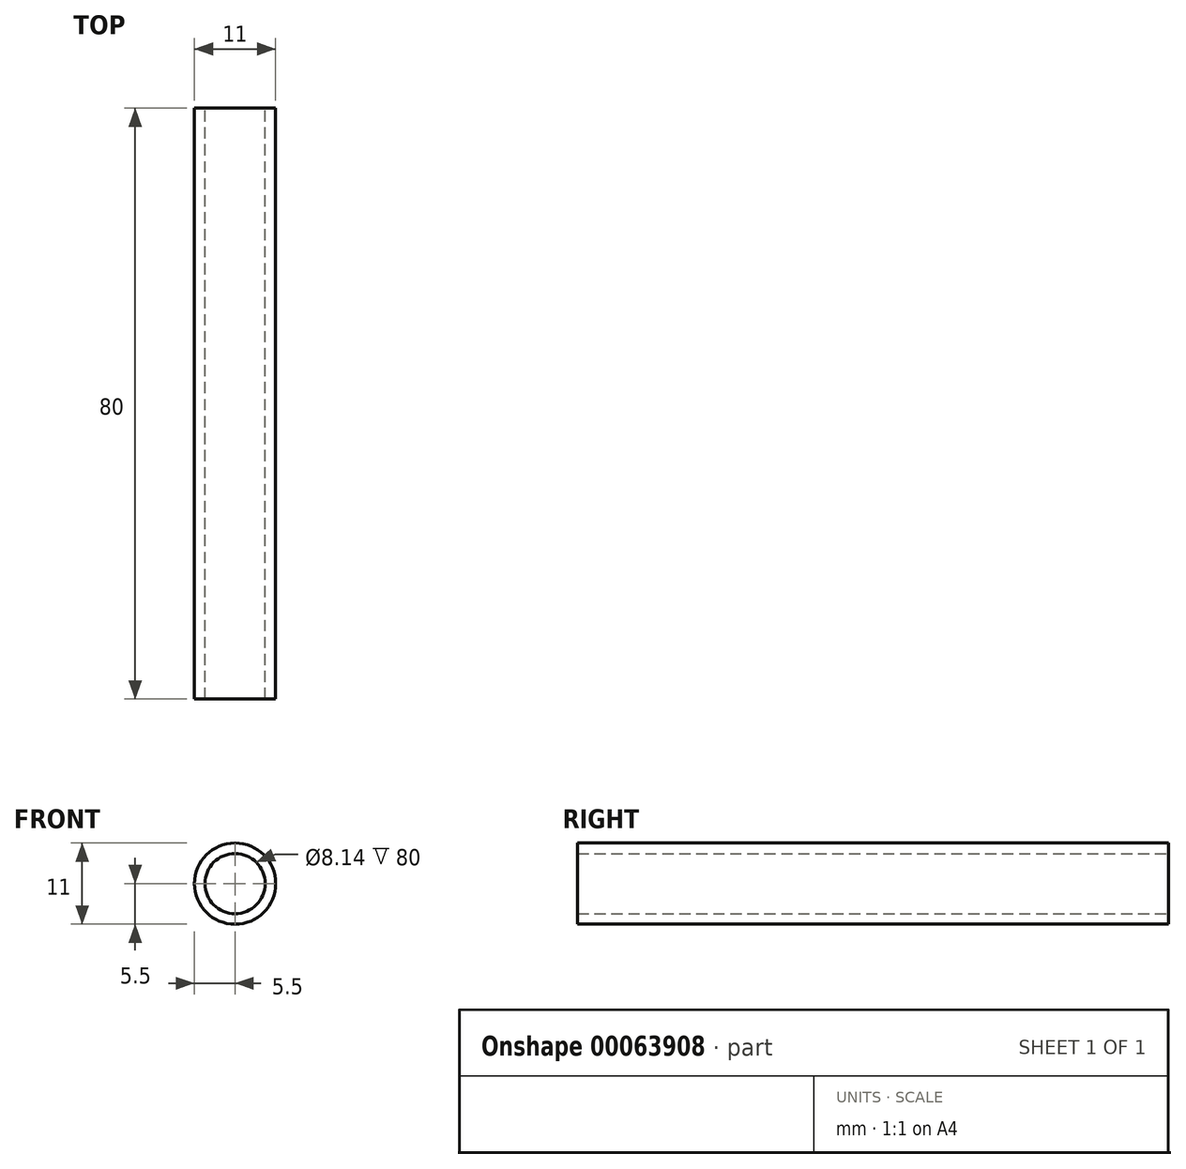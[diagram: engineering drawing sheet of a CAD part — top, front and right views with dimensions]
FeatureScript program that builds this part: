
annotation { "Feature Type Name" : "Feature", "Feature Type Description" : "" }
export const myFeature = defineFeature(function(context is Context, id is Id, definition is map)
    precondition{}
    {
        {
            var Q0;
            Q0=qCreatedBy(makeId("Front.planeOp"),FACE);
            var sketch = newSketch(context, id + "F0", { "sketchPlane" : qUnion([Q0])});
            skCircle(sketch, "E0", {"center": v(0, 0) * mm, "radius": 5.5 * mm});
            skCircle(sketch, "E1", {"center": v(0, 0) * mm, "radius": 4.07 * mm});
            skSolve(sketch);
        }
        {
            var Q0;
            Q0=makeQuery(id+"F0.imprint","IMPRINT",FACE,{"disambiguationData":[TD([[makeQuery(id+"F0.imprint","IMPRINT",EDGE,{"derivedFrom":sQuery(id+"F0.wireOp",EDGE,"E0")}),1.0]])]});
            extrude(context, id + "F1", {"entities" : qUnion([Q0]), "depth" : 80 * mm});
        }
    });
